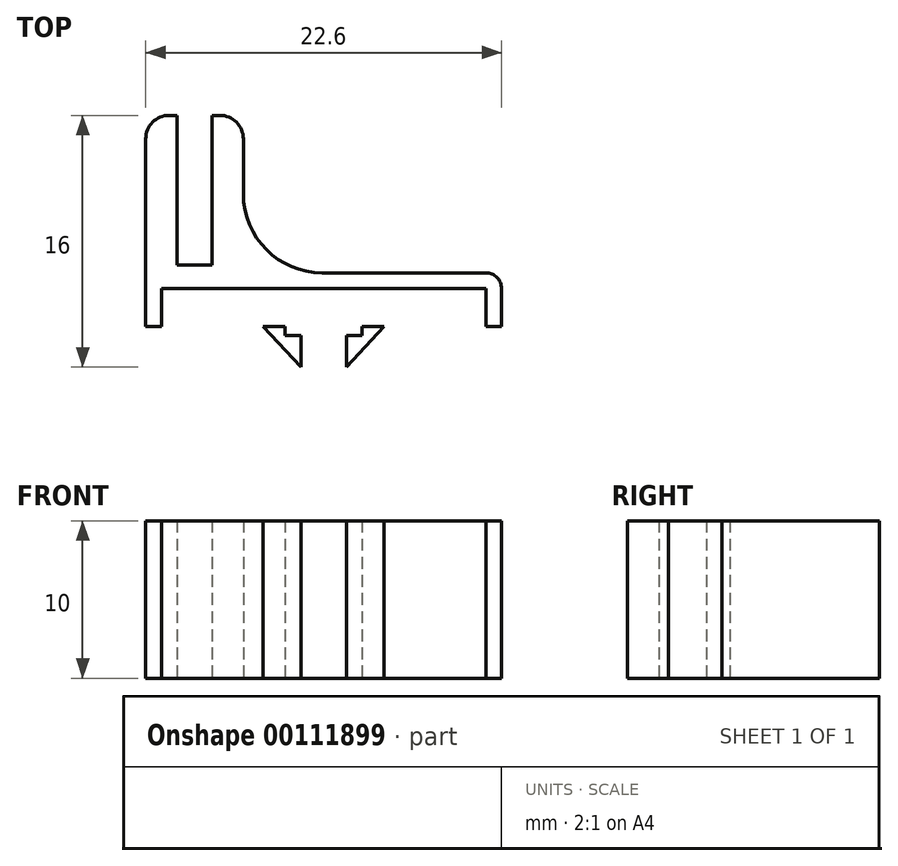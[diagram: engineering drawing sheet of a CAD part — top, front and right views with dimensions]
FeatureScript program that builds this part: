
annotation { "Feature Type Name" : "Feature", "Feature Type Description" : "" }
export const myFeature = defineFeature(function(context is Context, id is Id, definition is map)
    precondition{}
    {
        {
            var Q0;
            Q0=qCreatedBy(makeId("Top.planeOp"),FACE);
            var sketch = newSketch(context, id + "F0", { "sketchPlane" : qUnion([Q0])});
            skLineSegment(sketch, "E0.bottom", {"start": v(-10.3, -5.5) * mm, "end": v(10.3, -5.5) * mm});
            skLineSegment(sketch, "E0.right", {"start": v(10.3, -5.5) * mm, "end": v(10.3, -4.5) * mm});
            skLineSegment(sketch, "E1.bottom", {"start": v(10.3, -5.5) * mm, "end": v(11.3, -5.5) * mm});
            skLineSegment(sketch, "E1.top", {"start": v(10.3, -7.9) * mm, "end": v(11.3, -7.9) * mm});
            skLineSegment(sketch, "E1.left", {"start": v(10.3, -5.5) * mm, "end": v(10.3, -7.9) * mm});
            skLineSegment(sketch, "E1.right", {"start": v(11.3, -5.5) * mm, "end": v(11.3, -7.9) * mm});
            skArc(sketch, "E2", {"start": v(11.3, -5.5) * mm, "mid": v(11, -4.8) * mm, "end": v(10.3, -4.5) * mm});
            skLineSegment(sketch, "E3.bottom", {"start": v(-10.3, -5.5) * mm, "end": v(-11.3, -5.5) * mm});
            skLineSegment(sketch, "E3.top", {"start": v(-10.3, -7.9) * mm, "end": v(-11.3, -7.9) * mm});
            skLineSegment(sketch, "E3.left", {"start": v(-10.3, -5.5) * mm, "end": v(-10.3, -7.9) * mm});
            skLineSegment(sketch, "E3.right", {"start": v(-11.3, -5.5) * mm, "end": v(-11.3, -7.9) * mm});
            skLineSegment(sketch, "E4", {"start": v(-2.45, -5.5) * mm, "end": v(2.45, -5.5) * mm, "construction": true});
            skLineSegment(sketch, "E5.bottom", {"start": v(-2.45, -5.5) * mm, "end": v(-1.45, -5.5) * mm});
            skLineSegment(sketch, "E5.top", {"start": v(-2.45, -8.5) * mm, "end": v(-1.45, -8.5) * mm});
            skLineSegment(sketch, "E5.left", {"start": v(-2.45, -5.5) * mm, "end": v(-2.45, -8.5) * mm});
            skLineSegment(sketch, "E5.right", {"start": v(-1.45, -5.5) * mm, "end": v(-1.45, -8.5) * mm});
            skLineSegment(sketch, "E6.bottom", {"start": v(2.45, -5.5) * mm, "end": v(1.45, -5.5) * mm});
            skLineSegment(sketch, "E6.top", {"start": v(2.45, -8.5) * mm, "end": v(1.45, -8.5) * mm});
            skLineSegment(sketch, "E6.left", {"start": v(2.45, -5.5) * mm, "end": v(2.45, -8.5) * mm});
            skLineSegment(sketch, "E6.right", {"start": v(1.45, -5.5) * mm, "end": v(1.45, -8.5) * mm});
            skLineSegment(sketch, "E7", {"start": v(3.85, -7.9) * mm, "end": v(2.45, -7.9) * mm});
            skLineSegment(sketch, "E8", {"start": v(-2.45, -7.9) * mm, "end": v(-3.85, -7.9) * mm});
            skLineSegment(sketch, "E9", {"start": v(-2.45, -7.9) * mm, "end": v(2.45, -7.9) * mm, "construction": true});
            skLineSegment(sketch, "E10", {"start": v(1.45, -8.5) * mm, "end": v(1.45, -10.5) * mm});
            skLineSegment(sketch, "E11", {"start": v(1.45, -10.5) * mm, "end": v(3.85, -7.9) * mm});
            skLineSegment(sketch, "E12", {"start": v(-1.45, -8.5) * mm, "end": v(-1.45, -10.5) * mm});
            skLineSegment(sketch, "E13", {"start": v(-1.45, -10.5) * mm, "end": v(-3.85, -7.9) * mm});
            skLineSegment(sketch, "E14", {"start": v(-9.3, -4) * mm, "end": v(-7.1, -4) * mm});
            skLineSegment(sketch, "E15", {"start": v(-0.1, -4.5) * mm, "end": v(10.3, -4.5) * mm});
            skLineSegment(sketch, "E16", {"start": v(-11.3, -5.5) * mm, "end": v(-11.3, 4) * mm});
            skLineSegment(sketch, "E17", {"start": v(-9.3, -4) * mm, "end": v(-9.3, 5.5) * mm});
            skLineSegment(sketch, "E18", {"start": v(-9.3, 5.5) * mm, "end": v(-9.8, 5.5) * mm});
            skLineSegment(sketch, "E19", {"start": v(-7.1, -4) * mm, "end": v(-7.1, 5.5) * mm});
            skLineSegment(sketch, "E20", {"start": v(-5.1, 0.5) * mm, "end": v(-5.1, 4) * mm});
            skLineSegment(sketch, "E21", {"start": v(-6.6, 5.5) * mm, "end": v(-7.1, 5.5) * mm});
            skLineSegment(sketch, "E22", {"start": v(-9.3, 5.5) * mm, "end": v(-7.1, 5.5) * mm, "construction": true});
            skPoint(sketch, "E23.visualSharp", {"position": v(-11.3, -5.5) * mm});
            skPoint(sketch, "E24.visualSharp", {"position": v(-5.1, -4.5) * mm});
            skArc(sketch, "E24.filletArc", {"start": v(-5.1, 0.5) * mm, "mid": v(-3.64, -3.04) * mm, "end": v(-0.1, -4.5) * mm});
            skPoint(sketch, "E25.visualSharp", {"position": v(-11.3, 5.5) * mm});
            skArc(sketch, "E25.filletArc", {"start": v(-9.8, 5.5) * mm, "mid": v(-10.86, 5.06) * mm, "end": v(-11.3, 4) * mm});
            skPoint(sketch, "E26.visualSharp", {"position": v(-5.1, 5.5) * mm});
            skArc(sketch, "E26.filletArc", {"start": v(-5.1, 4) * mm, "mid": v(-5.54, 5.06) * mm, "end": v(-6.6, 5.5) * mm});
            skPoint(sketch, "E27", {"position": v(0, -7.9) * mm});
            skSolve(sketch);
        }
        {
            var Q0;
            Q0=makeQuery(id+"F0.imprint","IMPRINT",FACE,{"disambiguationData":[TD([[makeQuery(id+"F0.imprint","IMPRINT",EDGE,{"derivedFrom":sQuery(id+"F0.wireOp",EDGE,"E1.bottom")}),-1.0]])]});
            var Q1;
            Q1=makeQuery(id+"F0.imprint","IMPRINT",FACE,{"disambiguationData":[TD([[makeQuery(id+"F0.imprint","IMPRINT",EDGE,{"derivedFrom":sQuery(id+"F0.wireOp",EDGE,"E3.bottom")}),1.0]])]});
            var Q2;
            {var subQ1=sQuery(id+"F0.wireOp",EDGE,"E8");Q2=makeQuery(id+"F0.imprint","IMPRINT",FACE,{"disambiguationData":[TD([[makeQuery(id+"F0.imprint","IMPRINT",EDGE,{"derivedFrom":subQ1}),1.0]])]});}
            var Q3;
            {var subQ1=sQuery(id+"F0.wireOp",EDGE,"7c9eb7b9-ca48-4d36-bab2-391d59fa54ff");Q3=makeQuery(id+"F0.imprint","IMPRINT",FACE,{"disambiguationData":[TD([[makeQuery(id+"F0.imprint","IMPRINT",EDGE,{"derivedFrom":subQ1}),-1.0]])]});}
            var Q4;
            Q4=makeQuery(id+"F0.imprint","IMPRINT",FACE,{"disambiguationData":[TD([[makeQuery(id+"F0.imprint","IMPRINT",EDGE,{"derivedFrom":sQuery(id+"F0.wireOp",EDGE,"E0.left")}),1.0]])]});
            var Q5;
            Q5=makeQuery(id+"F0.imprint","IMPRINT",FACE,{"disambiguationData":[TD([[makeQuery(id+"F0.imprint","IMPRINT",EDGE,{"derivedFrom":sQuery(id+"F0.wireOp",EDGE,"E0.right")}),-1.0]])]});
            var Q6;
            {var subQ3=sQuery(id+"F0.wireOp",EDGE,"E5.bottom");Q6=makeQuery(id+"F0.imprint","IMPRINT",FACE,{"disambiguationData":[TD([[makeQuery(id+"F0.imprint","IMPRINT",EDGE,{"derivedFrom":subQ3}),-1.0]])]});}
            var Q7;
            {var subQ2=sQuery(id+"F0.wireOp",EDGE,"E6.bottom");Q7=makeQuery(id+"F0.imprint","IMPRINT",FACE,{"disambiguationData":[TD([[makeQuery(id+"F0.imprint","IMPRINT",EDGE,{"derivedFrom":subQ2}),1.0]])]});}
            var Q8;
            {var subQ0=sQuery(id+"F0.wireOp",EDGE,"7cf5e282-fc27-4f11-9d7e-3bad8ab92ec3");Q8=makeQuery(id+"F0.imprint","IMPRINT",FACE,{"disambiguationData":[TD([[makeQuery(id+"F0.imprint","IMPRINT",EDGE,{"derivedFrom":subQ0}),1.0]])]});}
            var Q9;
            {var subQ0=sQuery(id+"F0.wireOp",EDGE,"9b068b05-5ba9-4f17-919f-f73491ae4f90");Q9=makeQuery(id+"F0.imprint","IMPRINT",FACE,{"disambiguationData":[TD([[makeQuery(id+"F0.imprint","IMPRINT",EDGE,{"derivedFrom":subQ0}),-1.0]])]});}
            var Q10;
            {var subQ1=sQuery(id+"F0.wireOp",EDGE,"E0.left");Q10=makeQuery(id+"F0.imprint","IMPRINT",FACE,{"disambiguationData":[TD([[makeQuery(id+"F0.imprint","IMPRINT",EDGE,{"derivedFrom":subQ1}),-1.0]])]});}
            var Q11;
            {var subQ1=sQuery(id+"F0.wireOp",EDGE,"E0.right");Q11=makeQuery(id+"F0.imprint","IMPRINT",FACE,{"disambiguationData":[TD([[makeQuery(id+"F0.imprint","IMPRINT",EDGE,{"derivedFrom":subQ1}),1.0]])]});}
            var Q12;
            {var subQ0=sQuery(id+"F0.wireOp",EDGE,"E0.top");var subQ2=sQuery(id+"F0.wireOp",EDGE,"ccbefe15-ddc9-4d3c-9180-5a0c61267b28");var subQ4=makeQuery(id+"F0.imprint","INTERSECT",VERTEX,{"disambiguationData":[OD(0.0)],"derivedFrom":[subQ2,subQ0]});Q12=makeQuery(id+"F0.imprint","IMPRINT",FACE,{"disambiguationData":[TD([[makeQuery(id+"F0.imprint","IMPRINT",EDGE,{"disambiguationData":[TD([[subQ4,-1.0]])],"derivedFrom":subQ2}),1.0]])]});}
            var Q13;
            {var subQ2=sQuery(id+"F0.wireOp",EDGE,"E6.top");Q13=makeQuery(id+"F0.imprint","IMPRINT",FACE,{"disambiguationData":[TD([[makeQuery(id+"F0.imprint","IMPRINT",EDGE,{"derivedFrom":subQ2}),1.0]])]});}
            extrude(context, id + "F1", {"entities" : qUnion([Q0, Q1, Q2, Q3, Q4, Q5, Q6, Q7, Q8, Q9, Q10, Q11, Q12, Q13]), "depth" : 10 * mm});
        }
    });
